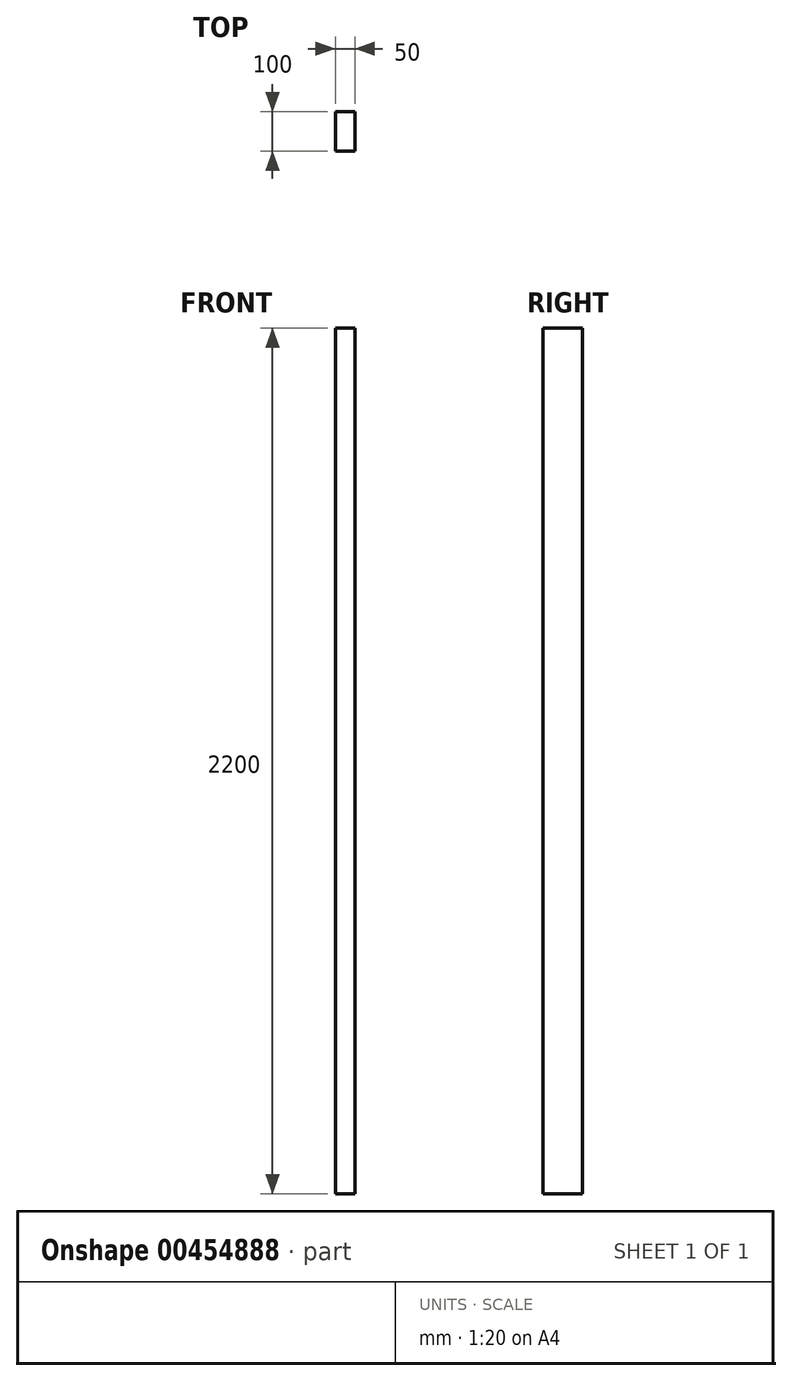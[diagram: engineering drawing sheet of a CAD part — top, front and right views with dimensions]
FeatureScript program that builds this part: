
annotation { "Feature Type Name" : "Feature", "Feature Type Description" : "" }
export const myFeature = defineFeature(function(context is Context, id is Id, definition is map)
    precondition{}
    {
        {
            var Q0;
            Q0=qCreatedBy(makeId("Top.planeOp"),FACE);
            var sketch = newSketch(context, id + "F0", { "sketchPlane" : qUnion([Q0])});
            skLineSegment(sketch, "E0.bottom", {"start": v(0, 0) * mm, "end": v(50, 0) * mm});
            skLineSegment(sketch, "E0.top", {"start": v(0, 100) * mm, "end": v(50, 100) * mm});
            skLineSegment(sketch, "E0.left", {"start": v(0, 0) * mm, "end": v(0, 100) * mm});
            skLineSegment(sketch, "E0.right", {"start": v(50, 0) * mm, "end": v(50, 100) * mm});
            skSolve(sketch);
        }
        {
            var Q0;
            Q0 = qSketchRegion(id + "F0", true);
            extrude(context, id + "F1", {"entities" : qUnion([Q0]), "depth" : 2200 * mm});
        }
    });
